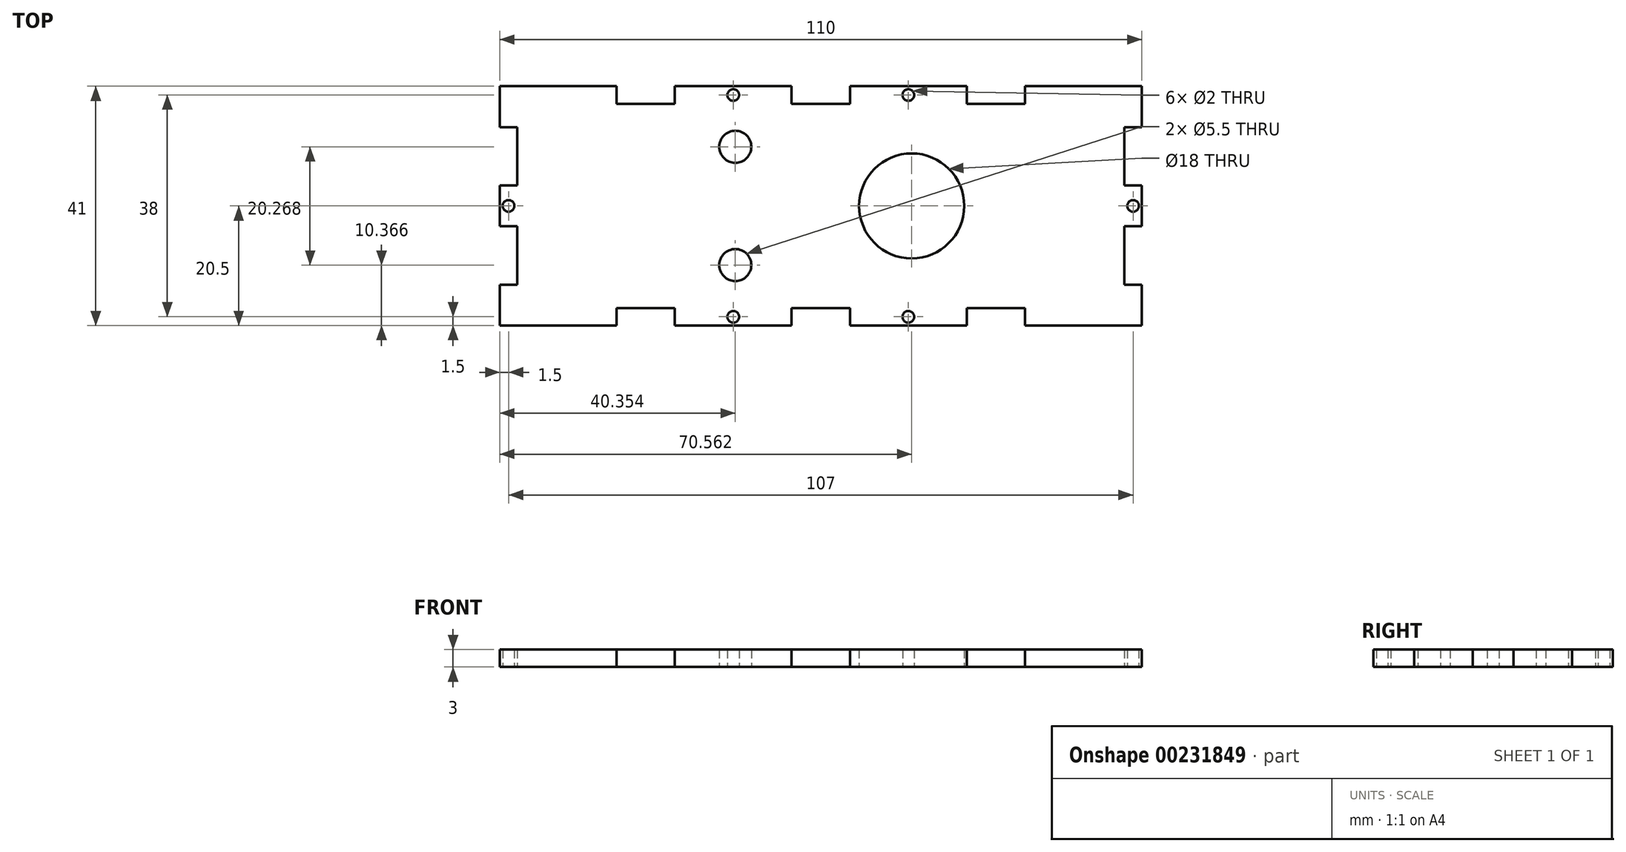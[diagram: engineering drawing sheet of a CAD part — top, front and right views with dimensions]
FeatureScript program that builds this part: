
annotation { "Feature Type Name" : "Feature", "Feature Type Description" : "" }
export const myFeature = defineFeature(function(context is Context, id is Id, definition is map)
    precondition{}
    {
        {
            var Q0;
            Q0=qCreatedBy(makeId("Top.planeOp"),FACE);
            var sketch = newSketch(context, id + "F0", { "sketchPlane" : qUnion([Q0])});
            skLineSegment(sketch, "E0", {"start": v(0, 0) * mm, "end": v(0, 7) * mm});
            skLineSegment(sketch, "E1", {"start": v(0, 7) * mm, "end": v(3, 7) * mm});
            skLineSegment(sketch, "E2", {"start": v(3, 7) * mm, "end": v(3, 17) * mm});
            skLineSegment(sketch, "E3", {"start": v(3, 17) * mm, "end": v(0, 17) * mm});
            skLineSegment(sketch, "E4", {"start": v(0, 17) * mm, "end": v(0, 24) * mm});
            skLineSegment(sketch, "E5", {"start": v(0, 24) * mm, "end": v(3, 24) * mm});
            skLineSegment(sketch, "E6", {"start": v(3, 24) * mm, "end": v(3, 34) * mm});
            skLineSegment(sketch, "E7", {"start": v(3, 34) * mm, "end": v(0, 34) * mm});
            skLineSegment(sketch, "E8", {"start": v(0, 34) * mm, "end": v(0, 41) * mm});
            skLineSegment(sketch, "E9", {"start": v(0, 0) * mm, "end": v(20, 0) * mm});
            skLineSegment(sketch, "E10", {"start": v(20, 0) * mm, "end": v(20, 3) * mm});
            skLineSegment(sketch, "E11", {"start": v(20, 3) * mm, "end": v(30, 3) * mm});
            skLineSegment(sketch, "E12", {"start": v(30, 3) * mm, "end": v(30, 0) * mm});
            skLineSegment(sketch, "E13", {"start": v(30, 0) * mm, "end": v(50, 0) * mm});
            skLineSegment(sketch, "E14", {"start": v(50, 0) * mm, "end": v(50, 3) * mm});
            skLineSegment(sketch, "E15", {"start": v(50, 3) * mm, "end": v(60, 3) * mm});
            skLineSegment(sketch, "E16", {"start": v(60, 0) * mm, "end": v(80, 0) * mm});
            skLineSegment(sketch, "E17", {"start": v(80, 0) * mm, "end": v(80, 3) * mm});
            skLineSegment(sketch, "E18", {"start": v(80, 3) * mm, "end": v(90, 3) * mm});
            skLineSegment(sketch, "E19", {"start": v(90, 3) * mm, "end": v(90, 0) * mm});
            skLineSegment(sketch, "E20", {"start": v(90, 0) * mm, "end": v(110, 0) * mm});
            skLineSegment(sketch, "E21", {"start": v(60, 3) * mm, "end": v(60, 0) * mm});
            skLineSegment(sketch, "E22", {"start": v(55, 3) * mm, "end": v(55, 34) * mm, "construction": true});
            skLineSegment(sketch, "E23.MirrorCS", {"start": v(107, 17) * mm, "end": v(110, 17) * mm});
            skLineSegment(sketch, "E24.MirrorCS", {"start": v(110, 24) * mm, "end": v(107, 24) * mm});
            skLineSegment(sketch, "E25.MirrorCS", {"start": v(110, 7) * mm, "end": v(107, 7) * mm});
            skLineSegment(sketch, "E26.MirrorCS", {"start": v(107, 34) * mm, "end": v(110, 34) * mm});
            skLineSegment(sketch, "E27.MirrorCS", {"start": v(107, 7) * mm, "end": v(107, 17) * mm});
            skLineSegment(sketch, "E28.MirrorCS", {"start": v(110, 17) * mm, "end": v(110, 24) * mm});
            skLineSegment(sketch, "E29.MirrorCS", {"start": v(110, 34) * mm, "end": v(110, 41) * mm});
            skLineSegment(sketch, "E30.MirrorCS", {"start": v(110, 0) * mm, "end": v(110, 7) * mm});
            skLineSegment(sketch, "E31.MirrorCS", {"start": v(107, 24) * mm, "end": v(107, 34) * mm});
            skLineSegment(sketch, "E32", {"start": v(0, 20.5) * mm, "end": v(124.38, 20.5) * mm, "construction": true});
            skPoint(sketch, "E32.endSnap0", {"position": v(110, 20.5) * mm});
            skLineSegment(sketch, "E33.MirrorCS", {"start": v(50, 41) * mm, "end": v(50, 38) * mm});
            skLineSegment(sketch, "E34.MirrorCS", {"start": v(60, 38) * mm, "end": v(60, 41) * mm});
            skLineSegment(sketch, "E35.MirrorCS", {"start": v(90, 38) * mm, "end": v(90, 41) * mm});
            skLineSegment(sketch, "E36.MirrorCS", {"start": v(30, 38) * mm, "end": v(30, 41) * mm});
            skLineSegment(sketch, "E37.MirrorCS", {"start": v(20, 41) * mm, "end": v(20, 38) * mm});
            skLineSegment(sketch, "E38.MirrorCS", {"start": v(80, 41) * mm, "end": v(80, 38) * mm});
            skLineSegment(sketch, "E39.MirrorCS", {"start": v(60, 41) * mm, "end": v(80, 41) * mm});
            skLineSegment(sketch, "E40.MirrorCS", {"start": v(80, 38) * mm, "end": v(90, 38) * mm});
            skLineSegment(sketch, "E41.MirrorCS", {"start": v(0, 41) * mm, "end": v(20, 41) * mm});
            skLineSegment(sketch, "E42.MirrorCS", {"start": v(90, 41) * mm, "end": v(110, 41) * mm});
            skLineSegment(sketch, "E43.MirrorCS", {"start": v(20, 38) * mm, "end": v(30, 38) * mm});
            skLineSegment(sketch, "E44.MirrorCS", {"start": v(50, 38) * mm, "end": v(60, 38) * mm});
            skLineSegment(sketch, "E45.MirrorCS", {"start": v(30, 41) * mm, "end": v(50, 41) * mm});
            skCircle(sketch, "E46", {"center": v(40, 1.5) * mm, "radius": 1 * mm});
            skPoint(sketch, "E46.centerSnap0", {"position": v(40, 0) * mm});
            skCircle(sketch, "E47.MirrorC", {"center": v(70, 1.5) * mm, "radius": 1 * mm});
            skCircle(sketch, "E48.MirrorC", {"center": v(70, 39.5) * mm, "radius": 1 * mm});
            skCircle(sketch, "E49.MirrorC", {"center": v(40, 39.5) * mm, "radius": 1 * mm});
            skCircle(sketch, "E50", {"center": v(1.5, 20.5) * mm, "radius": 1 * mm});
            skCircle(sketch, "E51.MirrorC", {"center": v(108.5, 20.5) * mm, "radius": 1 * mm});
            skLineSegment(sketch, "E52", {"start": v(25, 38) * mm, "end": v(25, 3) * mm, "construction": true});
            skPoint(sketch, "E53.centerSnap0", {"position": v(3, 29) * mm});
            skLineSegment(sketch, "E54", {"start": v(85, 38) * mm, "end": v(85, 3) * mm, "construction": true});
            skCircle(sketch, "E55", {"center": v(40.35, 30.63) * mm, "radius": 2.75 * mm});
            skCircle(sketch, "E56.MirrorC", {"center": v(40.35, 10.37) * mm, "radius": 2.75 * mm});
            skCircle(sketch, "E57", {"center": v(70.56, 20.5) * mm, "radius": 9 * mm});
            skSolve(sketch);
        }
        {
            var Q0;
            Q0=qSketchRegion(id+"F0",true);
            extrude(context, id + "F1", {"entities" : qUnion([Q0]), "endBound" : BoundingType.SYMMETRIC, "depth" : 3 * mm});
        }
    });
